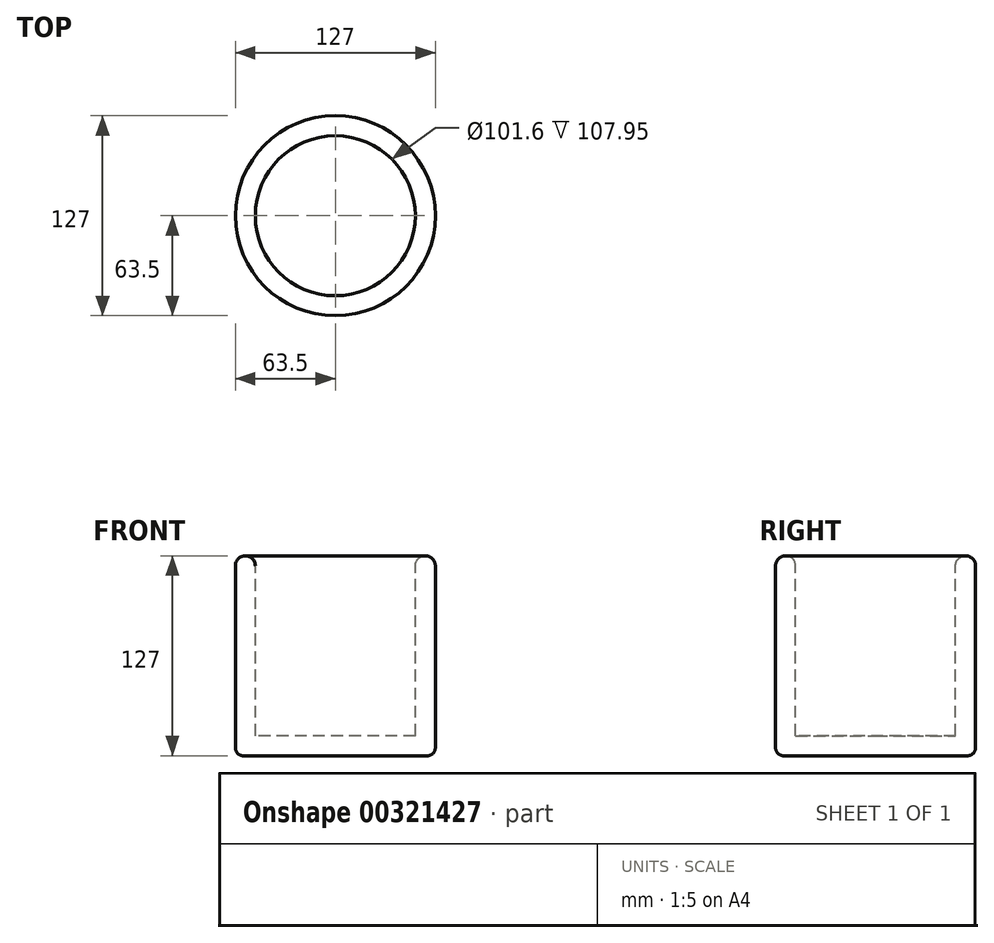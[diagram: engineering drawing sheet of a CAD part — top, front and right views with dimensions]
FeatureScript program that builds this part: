
annotation { "Feature Type Name" : "Feature", "Feature Type Description" : "" }
export const myFeature = defineFeature(function(context is Context, id is Id, definition is map)
    precondition{}
    {
        {
            var Q0;
            Q0=qCreatedBy(makeId("Front.planeOp"),FACE);
            var sketch = newSketch(context, id + "F0", { "sketchPlane" : qUnion([Q0])});
            skLineSegment(sketch, "E0", {"start": v(0, 0) * mm, "end": v(-63.5, 0) * mm});
            skLineSegment(sketch, "E1", {"start": v(-63.5, 0) * mm, "end": v(-63.5, 127) * mm});
            skLineSegment(sketch, "E2", {"start": v(-63.5, 127) * mm, "end": v(-50.8, 127) * mm});
            skLineSegment(sketch, "E3", {"start": v(-50.8, 127) * mm, "end": v(-50.8, 12.7) * mm});
            skLineSegment(sketch, "E4", {"start": v(-50.8, 12.7) * mm, "end": v(0, 12.7) * mm});
            skLineSegment(sketch, "E5", {"start": v(0, 12.7) * mm, "end": v(0, 0) * mm});
            skSolve(sketch);
        }
        {
            var Q0;
            Q0=makeQuery(id+"F0.imprint","IMPRINT",FACE,{"disambiguationData":[TD([[makeQuery(id+"F0.imprint","IMPRINT",EDGE,{"derivedFrom":sQuery(id+"F0.wireOp",EDGE,"E0")}),-1.0]])]});
            var Q1;
            Q1=sQuery(id+"F0.wireOp",EDGE,"E5");
            revolve(context, id + "F1", {"entities" : qUnion([Q0]), "axis" : qUnion([Q1]), "revolveType" : RevolveType.FULL});
        }
        {
            var Q0;
            Q0=makeQuery(id+"F1.opRevolve","SWEPT_EDGE",EDGE,{"disambiguationData":[OSD([sQuery(id+"F0.wireOp",EDGE,"E1"),sQuery(id+"F0.wireOp",EDGE,"E2")])]});
            var Q1;
            Q1=makeQuery(id+"F1.opRevolve","SWEPT_EDGE",EDGE,{"disambiguationData":[OSD([sQuery(id+"F0.wireOp",EDGE,"E2"),sQuery(id+"F0.wireOp",EDGE,"E3")])]});
            fillet(context, id + "F2", {"entities" : qUnion([Q0, Q1]), "radius" : 6.35 * mm, "tangentPropagation" : true, "allowEdgeOverflow" : false});
        }
        {
            var Q0;
            Q0=makeQuery(id+"F1.opRevolve","SWEPT_EDGE",EDGE,{"disambiguationData":[OSD([sQuery(id+"F0.wireOp",EDGE,"E0"),sQuery(id+"F0.wireOp",EDGE,"E1")])]});
            fillet(context, id + "F3", {"entities" : qUnion([Q0]), "radius" : 5.08 * mm, "tangentPropagation" : true, "allowEdgeOverflow" : false});
        }
    });
